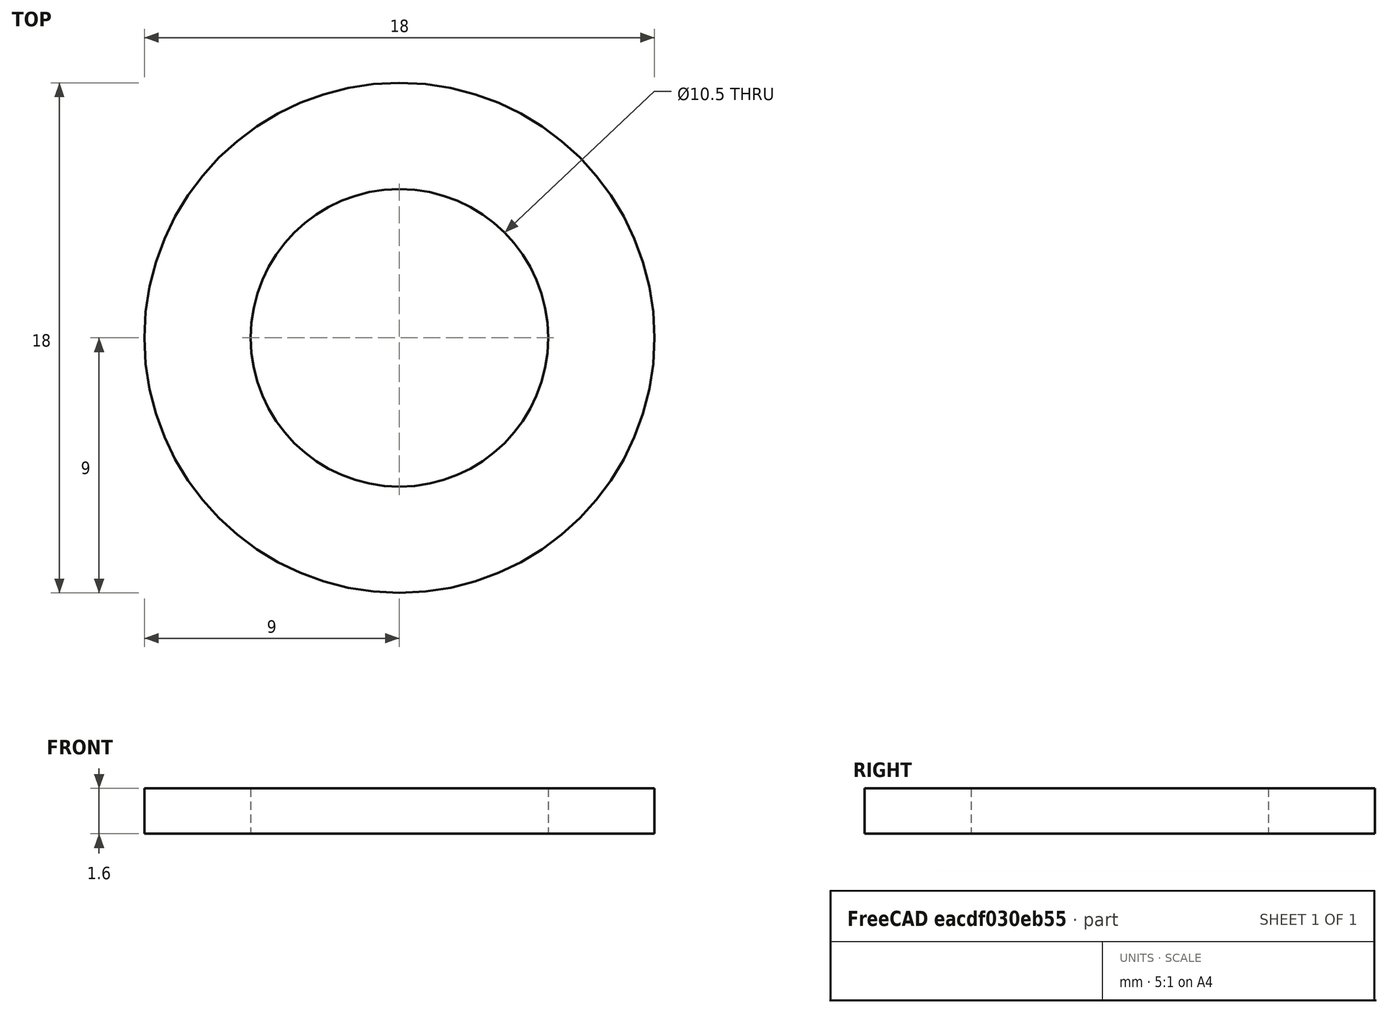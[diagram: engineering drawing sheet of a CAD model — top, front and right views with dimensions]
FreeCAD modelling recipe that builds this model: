
FCSTD DOCUMENT  (FreeCAD 0.14R3700 (Git))
Label: Scheibe DIN 433 - A 10,5
License: CC-BY 3.0
LicenseURL: http://creativecommons.org/licenses/by/3.0/
objects: Sketcher::SketchObject×1, PartDesign::Revolution×1, Part::Feature×1
note: 4 computed .brp shape members not serialized (recipe doc carries the construction recipe); baked Part::Feature solids carry a one-line shape summary decoded from their .brp

FEATURE [Sketcher::SketchObject] Sketch
  Placement = pos=(0,0,0) rot=(0.57735,0.57735,0.57735;2.0944rad)
  sketch-geometry (4):
    g0: LineSegment StartX=5.25 StartY=0 StartZ=0 EndX=9 EndY=0 EndZ=0
    g1: LineSegment StartX=9 StartY=0 StartZ=0 EndX=9 EndY=1.6 EndZ=0
    g2: LineSegment StartX=9 StartY=1.6 StartZ=0 EndX=5.25 EndY=1.6 EndZ=0
    g3: LineSegment StartX=5.25 StartY=1.6 StartZ=0 EndX=5.25 EndY=0 EndZ=0
  constraints (12):
    c: Coincident(g0,g1)
    c: Coincident(g1,g2)
    c: Coincident(g2,g3)
    c: Coincident(g3,g0)
    c: Horizontal(g0)
    c: Horizontal(g2)
    c: Vertical(g1)
    c: Vertical(g3)
    c: PointOnObject(g0,g-1)
    c: DistanceY(g1) = 1.6
    c: DistanceX(g-1,g2) = 5.25
    c: DistanceX(g-1,g1) = 9
FEATURE [PartDesign::Revolution] Revolution  label="Scheibe DIN 433 - A 10,5 #"
  Angle = 360
  Axis = (0,0,1)
  Base = (0,0,0)
  Placement = pos=(0,0,0) rot=(0.57735,0.57735,0.57735;2.0944rad)
  ReferenceAxis = -> Sketch [V_Axis]
  Reversed = true
  Sketch = -> Sketch
FEATURE [Part::Feature] Revolution001  label="Scheibe DIN 433 - A 10,5 #001"
  Placement = pos=(0,0,0) rot=(0.57735,0.57735,0.57735;2.0944rad)
  shape: bbox 18 x 18 x 1.6 mm, 4 faces (baked)
